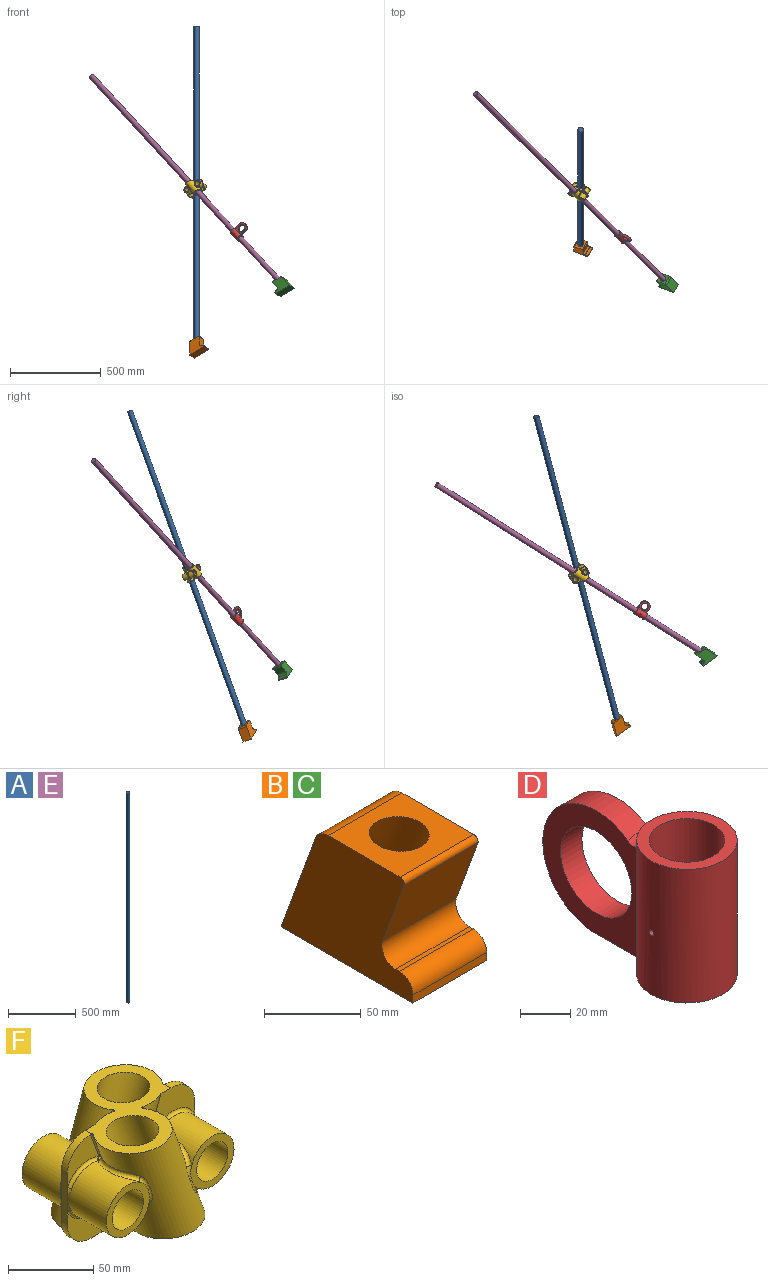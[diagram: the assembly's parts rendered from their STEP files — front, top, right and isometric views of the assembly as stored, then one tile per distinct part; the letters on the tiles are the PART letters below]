
ASSEMBLY  parts=6 mates=6
PART A: 3 faces, bbox 29.5x29.5x1900 mm
  f0: cylinder r=14.75mm len=1900mm, axis (0,0,-1), area 176086.3mm2, adj f1,f2
  f1: plane 29.5x29.5mm, normal (0,0,1), area 683.5mm2, adj f0
  f2: plane 29.5x29.5mm, normal (0,0,-1), area 683.5mm2, adj f0
PART B: 14 faces, bbox 54x96.3x85.3 mm
  f0: plane 30x28.19mm, normal (0,-0.34,0.94), area 706.9mm2, adj f1
  f1: cylinder r=15mm len=78.46mm, axis (0,0.34,-0.94), area 6318.7mm2, adj f0,f2
  f2: plane 54x52.59mm, normal (0,0,1), area 2087.6mm2, adj f1,f8,f9,f12,f13
  f3: plane 54x2.7mm, normal (0,0,1), area 145.9mm2, adj f8,f9,f10,f11
  f4: plane 68.44x54mm, normal (0,0.94,0.34), area 3933.1mm2, adj f7,f8,f9,f12
  f5: plane 54x42.55mm, normal (0,-0.94,-0.34), area 2445.4mm2, adj f8,f9,f11,f13
  f6: plane 54x5mm, normal (0,-1,0), area 270mm2, adj f7,f8,f9,f10
  f7: plane 96.29x54mm, normal (0,0,-1), area 5199.8mm2, adj f4,f6,f8,f9
  f8: plane 96.29x75mm, normal (1,0,0), area 5246.8mm2, adj f2,f3,f4,f5,f6,f7,f10,f11
  f9: plane 96.29x75mm, normal (-1,0,0), area 5246.8mm2, adj f2,f3,f4,f5,f6,f7,f10,f11
  f10: cylinder r=10mm len=54mm, axis (-1,0,0), area 848.2mm2, adj f3,f6,f8,f9
  f11: cylinder r=10mm len=54mm, axis (1,0,0), area 1036.7mm2, adj f3,f5,f8,f9
  f12: cylinder r=9.96mm len=54mm, axis (1,0,0), area 657.4mm2, adj f2,f4,f8,f9
  f13: cylinder r=3mm len=54mm, axis (1,0,0), area 311mm2, adj f2,f5,f8,f9
PART C: same geometry as B
PART D: 12 faces, bbox 40.4x95.4x65.4 mm
  f0: cylinder r=30mm len=60mm, axis (-1,0,0), area 1353mm2, adj f1,f2,f3,f8
  f1: plane 60.37x52.92mm, normal (1,0,0), area 1445.3mm2, adj f0,f3,f4,f8,f9
  f2: plane 60.37x52.92mm, normal (-1,0,0), area 1445.3mm2, adj f0,f3,f4,f8,f10
  f3: plane 65x40mm, normal (0,0,-1), area 857.2mm2, adj f0,f1,f2,f5,f6,f9,f10
  f4: cylinder r=20mm len=40mm, axis (-1,0,0), area 1508mm2, adj f1,f2
  f5: cylinder r=15mm len=65mm, axis (0,0,-1), area 6121.2mm2, adj f3,f7,f11
  f6: cylinder r=20mm len=65mm, axis (0,0,-1), area 7104.6mm2, adj f3,f7,f8,f9,f10,f11
  f7: plane 40x40mm, normal (0,0,1), area 549.8mm2, adj f5,f6
  f8: bspline ~24.2x11.43mm, area 148.5mm2, adj f0,f1,f2,f6,f9,f10
  f9: cylinder r=5mm len=56.77mm, axis (0,0,-1), area 306.9mm2, adj f1,f3,f6,f8
  f10: cylinder r=5mm len=56.77mm, axis (0,0,-1), area 306.9mm2, adj f2,f3,f6,f8
  f11: cylinder r=1.25mm len=5mm, axis (1,0,0), area 39.3mm2, adj f5,f6
PART E: same geometry as A
PART F: 98 faces, bbox 133.8x101.8x127.7 mm
  f0: cylinder r=22.5mm len=30.46mm, axis (-0.34,0,-0.94), area 212.9mm2, adj f27,f39,f41
  f1: cylinder r=22.5mm len=30.46mm, axis (-0.34,0,-0.94), area 212.9mm2, adj f21,f48,f51
  f2: cylinder r=22.5mm len=105.86mm, axis (-0.34,0,-0.94), area 5549.6mm2, adj f21,f27,f35,f37,f43,f45,f47,f53
  f3: cylinder r=22.5mm len=30.46mm, axis (0.34,0,-0.94), area 212.9mm2, adj f27,f34,f37
  f4: cylinder r=22.5mm len=30.46mm, axis (0.34,0,-0.94), area 212.9mm2, adj f21,f44,f47
  f5: cylinder r=22.5mm len=105.86mm, axis (0.34,0,-0.94), area 5549.6mm2, adj f21,f27,f38,f39,f42,f49,f51,f52
  f6: cylinder r=18mm len=36mm, axis (0,1,0), area 2341.1mm2, adj f11,f54,f55,f56,f59,f60,f64
  f7: cylinder r=18mm len=36mm, axis (0,1,0), area 2341.1mm2, adj f15,f65,f66,f69,f71,f74,f75
  f8: cylinder r=13mm len=70mm, axis (0,1,0), area 5717.7mm2, adj f10,f11
  f9: cylinder r=18mm len=36mm, axis (0,1,0), area 2341.1mm2, adj f10,f87,f88,f91,f92,f94,f95
  f10: plane 36.68x36.68mm, normal (0,-1,0), area 486.9mm2, adj f8,f9,f93
  f11: plane 36.68x36.68mm, normal (0,1,0), area 486.9mm2, adj f6,f8,f63
  f12: cylinder r=13mm len=70mm, axis (0,1,0), area 5717.7mm2, adj f14,f15
  f13: cylinder r=18mm len=36mm, axis (0,1,0), area 2341.1mm2, adj f14,f76,f77,f80,f81,f83,f84
  f14: plane 36.68x36.68mm, normal (0,-1,0), area 486.9mm2, adj f12,f13,f82
  f15: plane 36.68x36.68mm, normal (0,1,0), area 486.9mm2, adj f7,f12,f70
  f16: plane 36.04x6.04mm, normal (1,0,0), area 175mm2, adj f17,f18,f19,f20,f31,f32,f65,f74
  f17: plane 37.46x28.78mm, normal (0,1,0), area 582.5mm2, adj f16,f27,f31,f34,f35,f72,f75
  f18: plane 28.77x26.23mm, normal (0,-1,0), area 371.1mm2, adj f16,f31,f42,f83,f86
  f19: plane 28.77x26.23mm, normal (0,1,0), area 371.1mm2, adj f16,f32,f53,f66,f68
  f20: plane 37.46x28.78mm, normal (0,-1,0), area 582.5mm2, adj f16,f21,f32,f48,f49,f77,f78
  f21: plane 101.84x97.02mm, normal (0,0,1), area 1918.1mm2, adj f1,f2,f4,f5,f20,f23,f28,f29
  f22: plane 28.77x26.23mm, normal (0,1,0), area 371.1mm2, adj f26,f30,f43,f55,f58
  f23: plane 37.46x28.78mm, normal (0,1,0), area 582.5mm2, adj f21,f26,f33,f44,f45,f59,f61
  f24: plane 28.77x26.23mm, normal (0,-1,0), area 371.1mm2, adj f26,f33,f52,f94,f97
  f25: plane 37.46x28.78mm, normal (0,-1,0), area 582.5mm2, adj f26,f27,f30,f38,f41,f88,f89
  f26: plane 36.04x6.04mm, normal (-1,0,0), area 175mm2, adj f22,f23,f24,f25,f30,f33,f54,f56
  f27: plane 101.84x97.02mm, normal (0,0,-1), area 1918.1mm2, adj f0,f2,f3,f5,f17,f25,f28,f29
  f28: cylinder r=15mm len=85.26mm, axis (-0.34,0,-0.94), area 7522.2mm2, adj f21,f27
  f29: cylinder r=15mm len=85.26mm, axis (0.34,0,-0.94), area 7522.2mm2, adj f21,f27
  f30: cylinder r=20mm len=20mm, axis (0,-1,0), area 157.1mm2, adj f22,f25,f26,f27,f43
  f31: cylinder r=20mm len=20mm, axis (0,-1,0), area 157.1mm2, adj f16,f17,f18,f27,f42
  f32: cylinder r=20mm len=20mm, axis (0,1,0), area 157.1mm2, adj f16,f19,f20,f21,f53
  f33: cylinder r=20mm len=20mm, axis (0,1,0), area 157.1mm2, adj f21,f23,f24,f26,f52
  f34: cylinder r=1mm len=25.48mm, axis (0.34,0,-0.94), area 12.5mm2, adj f3,f17,f27,f36
  f35: cylinder r=1mm len=3.33mm, axis (-0.34,0,-0.94), area 7mm2, adj f2,f17,f36,f72
  f36: sphere r=1mm, area 0.2mm2, adj f34,f35,f37
  f37: bspline ~30.26x10.36mm, area 53.7mm2, adj f2,f3,f27,f36
  f38: cylinder r=1mm len=3.33mm, axis (0.34,0,-0.94), area 7mm2, adj f5,f25,f40,f89
  f39: bspline ~29.49x10.35mm, area 53.7mm2, adj f0,f5,f27,f40
  f40: sphere r=1mm, area 0.4mm2, adj f38,f39,f41
  f41: cylinder r=1mm len=25.48mm, axis (-0.34,0,-0.94), area 12.5mm2, adj f0,f25,f27,f40
  f42: cylinder r=1mm len=18.98mm, axis (0.34,0,-0.94), area 43.4mm2, adj f5,f18,f27,f31,f86
  f43: cylinder r=1mm len=18.98mm, axis (-0.34,0,-0.94), area 43.4mm2, adj f2,f22,f27,f30,f58
  f44: cylinder r=1mm len=25.48mm, axis (0.34,0,-0.94), area 12.5mm2, adj f4,f21,f23,f46
  f45: cylinder r=1mm len=3.33mm, axis (-0.34,0,-0.94), area 7mm2, adj f2,f23,f46,f61
  f46: sphere r=1mm, area 0.4mm2, adj f44,f45,f47
  f47: bspline ~32.76x10.98mm, area 53.7mm2, adj f2,f4,f21,f46
  f48: cylinder r=1mm len=25.48mm, axis (-0.34,0,-0.94), area 12.5mm2, adj f1,f20,f21,f50
  f49: cylinder r=1mm len=3.33mm, axis (0.34,0,-0.94), area 7mm2, adj f5,f20,f50,f78
  f50: sphere r=1mm, area 0.2mm2, adj f48,f49,f51
  f51: bspline ~30.3x10.19mm, area 53.7mm2, adj f1,f5,f21,f50
  f52: cylinder r=1mm len=18.98mm, axis (0.34,0,-0.94), area 43.4mm2, adj f5,f21,f24,f33,f97
  f53: cylinder r=1mm len=18.98mm, axis (-0.34,0,-0.94), area 43.4mm2, adj f2,f19,f21,f32,f68
  f54: bspline ~9.15x2.2mm, area 8.2mm2, adj f6,f26,f55
  f55: torus R=20mm, axis (0,-1,0), area 87.4mm2, adj f6,f22,f54,f57
  f56: bspline ~9.15x2.2mm, area 8.2mm2, adj f6,f26,f59
  f57: bspline ~5.11x2.31mm, area 4.2mm2, adj f55,f58,f60
  f58: bspline ~3.23x2.55mm, area 2.7mm2, adj f22,f43,f57,f60
  f59: torus R=20mm, axis (0,-1,0), area 128.5mm2, adj f6,f23,f56,f62
  f60: bspline ~33.99x11.28mm, area 138.3mm2, adj f2,f6,f57,f58,f63
  f61: bspline ~3.08x2.39mm, area 2.7mm2, adj f23,f45,f62,f64
  f62: bspline ~4.53x3.27mm, area 4.2mm2, adj f59,f61,f64
  f63: bspline ~23.33x11.21mm, area 57.2mm2, adj f2,f11,f60,f64
  f64: bspline ~34.21x11.22mm, area 138.3mm2, adj f2,f6,f61,f62,f63
  f65: bspline ~9.15x2.2mm, area 8.2mm2, adj f7,f16,f66
  f66: torus R=20mm, axis (0,-1,0), area 87.4mm2, adj f7,f19,f65,f67
  f67: bspline ~5.11x2.31mm, area 4.2mm2, adj f66,f68,f69
  f68: bspline ~3.23x2.55mm, area 2.7mm2, adj f19,f53,f67,f69
  f69: bspline ~34.28x11.7mm, area 138.3mm2, adj f2,f7,f67,f68,f70
  f70: bspline ~23.33x11.21mm, area 57.2mm2, adj f2,f15,f69,f71
  f71: bspline ~33.83x10.9mm, area 138.3mm2, adj f2,f7,f70,f72,f73
  f72: bspline ~3.08x2.39mm, area 2.7mm2, adj f17,f35,f71,f73
  f73: bspline ~4.53x3.27mm, area 4.2mm2, adj f71,f72,f75
  f74: bspline ~9.15x2.2mm, area 8.2mm2, adj f7,f16,f75
  f75: torus R=20mm, axis (0,-1,0), area 128.5mm2, adj f7,f17,f73,f74
  f76: bspline ~9.15x2.2mm, area 8.2mm2, adj f13,f16,f77
  f77: torus R=20mm, axis (0,-1,0), area 128.5mm2, adj f13,f20,f76,f79
  f78: bspline ~3.08x2.39mm, area 2.7mm2, adj f20,f49,f79,f80
  f79: bspline ~4.53x3.27mm, area 4.2mm2, adj f77,f78,f80
  f80: bspline ~34.21x11.22mm, area 138.3mm2, adj f5,f13,f78,f79,f82
  f81: bspline ~9.15x2.2mm, area 8.2mm2, adj f13,f16,f83
  f82: bspline ~23.33x11.21mm, area 57.2mm2, adj f5,f14,f80,f84
  f83: torus R=20mm, axis (0,-1,0), area 87.4mm2, adj f13,f18,f81,f85
  f84: bspline ~33.99x11.28mm, area 138.3mm2, adj f5,f13,f82,f85,f86
  f85: bspline ~5.11x2.31mm, area 4.2mm2, adj f83,f84,f86
  f86: bspline ~3.23x2.55mm, area 2.7mm2, adj f18,f42,f84,f85
  f87: bspline ~9.15x2.2mm, area 8.2mm2, adj f9,f26,f88
  f88: torus R=20mm, axis (0,-1,0), area 128.5mm2, adj f9,f25,f87,f90
  f89: bspline ~3.08x2.39mm, area 2.7mm2, adj f25,f38,f90,f91
  f90: bspline ~4.53x3.27mm, area 4.2mm2, adj f88,f89,f91
  f91: bspline ~33.83x10.9mm, area 138.3mm2, adj f5,f9,f89,f90,f93
  f92: bspline ~9.15x2.2mm, area 8.2mm2, adj f9,f26,f94
  f93: bspline ~23.33x11.21mm, area 57.2mm2, adj f5,f10,f91,f95
  f94: torus R=20mm, axis (0,-1,0), area 87.4mm2, adj f9,f24,f92,f96
  f95: bspline ~34.28x11.7mm, area 138.3mm2, adj f5,f9,f93,f96,f97
  f96: bspline ~5.11x2.31mm, area 4.2mm2, adj f94,f95,f97
  f97: bspline ~3.23x2.55mm, area 2.7mm2, adj f24,f52,f95,f96
PLACE A rot(axis=(-0.56,-0.14,-0.82),35.1deg) t=(-248.48,-294.94,-957.68)mm
PLACE B rot(axis=(-0.5,0,0.86),71.9deg) t=(-257.97,-322.86,-959.51)mm
PLACE C rot(axis=(0,-0.34,-0.94),119deg) t=(259.62,-483.75,-627)mm
PLACE D rot(axis=(0.83,0.54,0.11),129.2deg) t=(0.51,-239.07,-279.16)mm
PLACE E rot(axis=(-0.38,0.24,0.89),158.3deg) t=(242.95,-500.22,-609.01)mm
PLACE F rot(axis=(-0.57,-0.57,-0.59),42.7deg) t=(-256.96,15.6,-59.73)mm
MATE parallel B.f7 <-> C.f7  axis (0.3,-0.48,-0.83) through (-235.15,-304.34,-961.94)mm
MATE revolute E.f0 <-> F.f3  axis (0.56,-0.55,-0.61) through (-291.25,26.67,-26.34)mm
MATE slider E.f0 <-> D.f5  axis (0.56,-0.55,-0.61) through (-291.25,26.67,-26.34)mm
MATE revolute E.f0 <-> C.f1  axis (0.56,-0.55,-0.61) through (242.95,-500.22,-609.01)mm
MATE revolute F.f0 <-> A.f0  axis (0,-0.34,-0.94) through (-248.48,29.98,-64.97)mm
MATE revolute B.f1 <-> A.f0  axis (0,0.34,0.94) through (-248.48,-294.94,-957.68)mm
